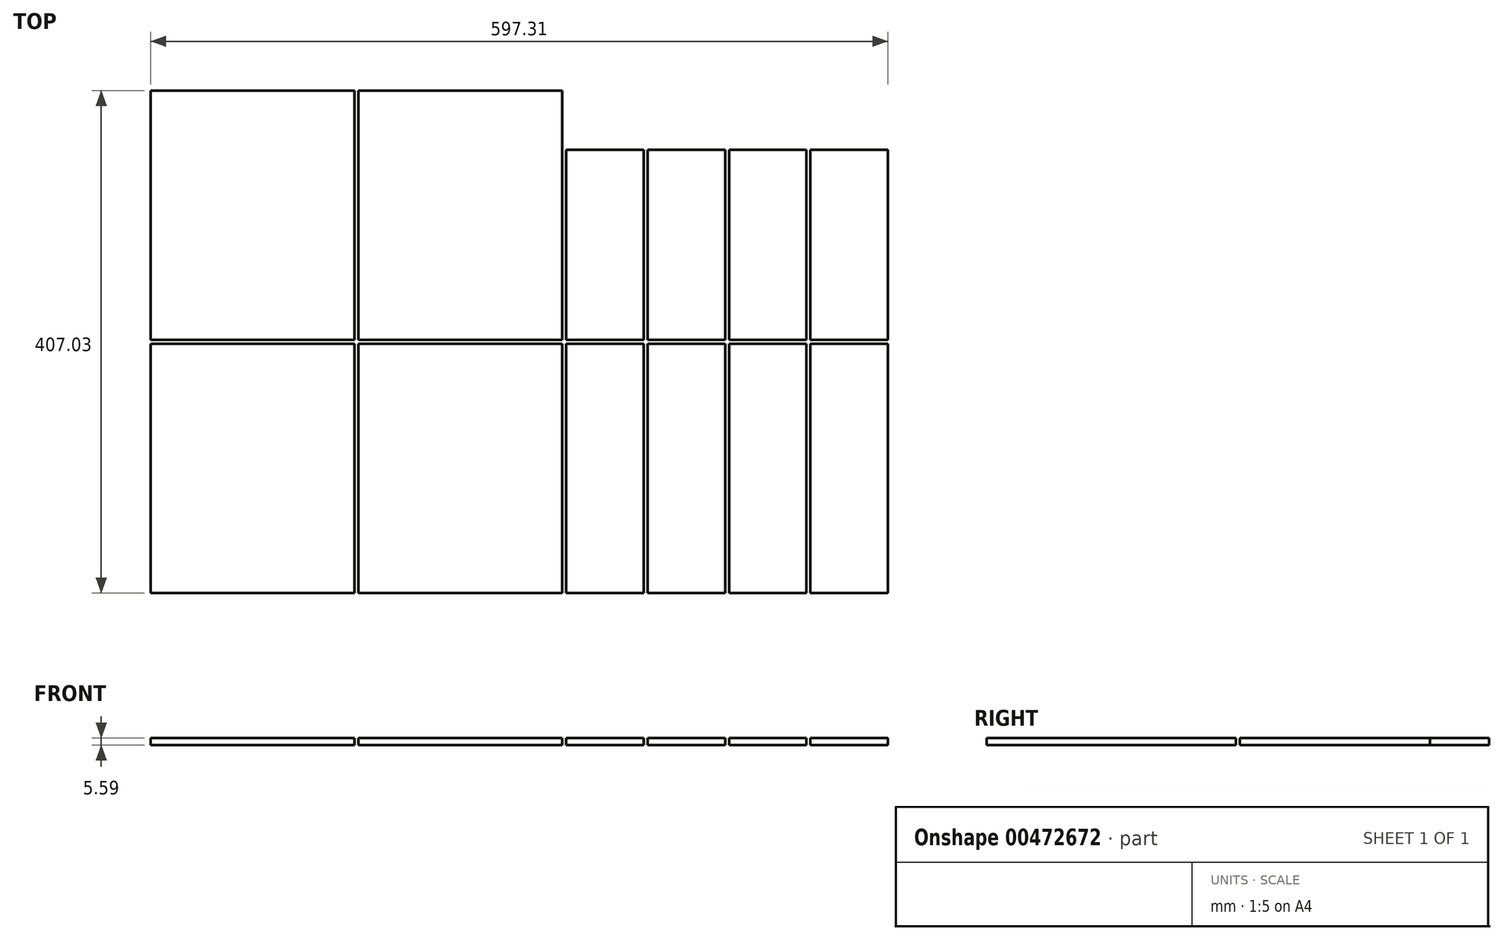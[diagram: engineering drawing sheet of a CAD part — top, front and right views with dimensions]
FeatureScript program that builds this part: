
annotation { "Feature Type Name" : "Feature", "Feature Type Description" : "" }
export const myFeature = defineFeature(function(context is Context, id is Id, definition is map)
    precondition{}
    {
        {
            var Q0;
            Q0=qCreatedBy(makeId("Top.planeOp"),FACE);
            var sketch = newSketch(context, id + "F0", { "sketchPlane" : qUnion([Q0])});
            skLineSegment(sketch, "E0.bottom", {"start": v(0, 0) * mm, "end": v(165.1, 0) * mm});
            skLineSegment(sketch, "E0.top", {"start": v(0, 201.93) * mm, "end": v(165.1, 201.93) * mm});
            skLineSegment(sketch, "E0.left", {"start": v(0, 0) * mm, "end": v(0, 201.93) * mm});
            skLineSegment(sketch, "E0.right", {"start": v(165.1, 0) * mm, "end": v(165.1, 201.93) * mm});
            skLineSegment(sketch, "E1.bottom", {"start": v(168.27, 0) * mm, "end": v(333.38, 0) * mm});
            skLineSegment(sketch, "E1.top", {"start": v(168.27, 201.93) * mm, "end": v(333.38, 201.93) * mm});
            skLineSegment(sketch, "E1.left", {"start": v(168.27, 0) * mm, "end": v(168.27, 201.93) * mm});
            skLineSegment(sketch, "E1.right", {"start": v(333.38, 0) * mm, "end": v(333.37, 201.93) * mm});
            skLineSegment(sketch, "E2.bottom", {"start": v(0, 205.1) * mm, "end": v(165.1, 205.1) * mm});
            skLineSegment(sketch, "E2.top", {"start": v(0, 407.04) * mm, "end": v(165.1, 407.04) * mm});
            skLineSegment(sketch, "E2.left", {"start": v(0, 205.1) * mm, "end": v(0, 407.04) * mm});
            skLineSegment(sketch, "E2.right", {"start": v(165.1, 205.1) * mm, "end": v(165.1, 407.04) * mm});
            skLineSegment(sketch, "E3.bottom", {"start": v(168.27, 205.1) * mm, "end": v(333.37, 205.1) * mm});
            skLineSegment(sketch, "E3.top", {"start": v(168.27, 407.04) * mm, "end": v(333.37, 407.04) * mm});
            skLineSegment(sketch, "E3.left", {"start": v(168.28, 205.1) * mm, "end": v(168.27, 407.04) * mm});
            skLineSegment(sketch, "E3.right", {"start": v(333.37, 205.1) * mm, "end": v(333.37, 407.04) * mm});
            skLineSegment(sketch, "E4", {"start": v(168.27, 205.1) * mm, "end": v(165.1, 205.1) * mm, "construction": true});
            skLineSegment(sketch, "E5", {"start": v(168.27, 205.1) * mm, "end": v(168.27, 201.93) * mm, "construction": true});
            skLineSegment(sketch, "E6.bottom", {"start": v(336.55, 0) * mm, "end": v(399.36, 0) * mm});
            skLineSegment(sketch, "E6.top", {"start": v(336.55, 201.93) * mm, "end": v(399.36, 201.93) * mm});
            skLineSegment(sketch, "E6.left", {"start": v(336.55, 0) * mm, "end": v(336.55, 201.93) * mm});
            skLineSegment(sketch, "E6.right", {"start": v(399.36, 0) * mm, "end": v(399.36, 201.93) * mm});
            skLineSegment(sketch, "E7.bottom", {"start": v(336.55, 205.1) * mm, "end": v(399.36, 205.1) * mm});
            skLineSegment(sketch, "E7.top", {"start": v(336.55, 359.03) * mm, "end": v(399.36, 359.03) * mm});
            skLineSegment(sketch, "E7.left", {"start": v(336.55, 205.1) * mm, "end": v(336.55, 359.03) * mm});
            skLineSegment(sketch, "E7.right", {"start": v(399.36, 205.1) * mm, "end": v(399.36, 359.03) * mm});
            skLineSegment(sketch, "E8.1.0.0", {"start": v(402.53, 359.03) * mm, "end": v(465.34, 359.03) * mm});
            skLineSegment(sketch, "E8.1.0.1", {"start": v(465.34, 205.1) * mm, "end": v(465.34, 359.03) * mm});
            skLineSegment(sketch, "E8.1.0.2", {"start": v(402.53, 205.1) * mm, "end": v(402.53, 359.03) * mm});
            skLineSegment(sketch, "E8.1.0.3", {"start": v(402.53, 205.1) * mm, "end": v(465.34, 205.1) * mm});
            skLineSegment(sketch, "E8.1.0.4", {"start": v(402.53, 201.93) * mm, "end": v(465.34, 201.93) * mm});
            skLineSegment(sketch, "E8.1.0.5", {"start": v(402.53, 0) * mm, "end": v(402.53, 201.93) * mm});
            skLineSegment(sketch, "E8.1.0.6", {"start": v(465.34, 0) * mm, "end": v(465.34, 201.93) * mm});
            skLineSegment(sketch, "E8.1.0.7", {"start": v(402.53, 0) * mm, "end": v(465.34, 0) * mm});
            skLineSegment(sketch, "E8.2.0.0", {"start": v(468.52, 359.03) * mm, "end": v(531.33, 359.03) * mm});
            skLineSegment(sketch, "E8.2.0.1", {"start": v(531.33, 205.1) * mm, "end": v(531.33, 359.03) * mm});
            skLineSegment(sketch, "E8.2.0.2", {"start": v(468.52, 205.1) * mm, "end": v(468.52, 359.03) * mm});
            skLineSegment(sketch, "E8.2.0.3", {"start": v(468.52, 205.1) * mm, "end": v(531.33, 205.1) * mm});
            skLineSegment(sketch, "E8.2.0.4", {"start": v(468.52, 201.93) * mm, "end": v(531.33, 201.93) * mm});
            skLineSegment(sketch, "E8.2.0.5", {"start": v(468.52, 0) * mm, "end": v(468.52, 201.93) * mm});
            skLineSegment(sketch, "E8.2.0.6", {"start": v(531.33, 0) * mm, "end": v(531.33, 201.93) * mm});
            skLineSegment(sketch, "E8.2.0.7", {"start": v(468.52, 0) * mm, "end": v(531.33, 0) * mm});
            skLineSegment(sketch, "E8.3.0.0", {"start": v(534.5, 359.03) * mm, "end": v(597.31, 359.03) * mm});
            skLineSegment(sketch, "E8.3.0.1", {"start": v(597.31, 205.1) * mm, "end": v(597.31, 359.03) * mm});
            skLineSegment(sketch, "E8.3.0.2", {"start": v(534.5, 205.1) * mm, "end": v(534.5, 359.03) * mm});
            skLineSegment(sketch, "E8.3.0.3", {"start": v(534.5, 205.1) * mm, "end": v(597.31, 205.1) * mm});
            skLineSegment(sketch, "E8.3.0.4", {"start": v(534.5, 201.93) * mm, "end": v(597.31, 201.93) * mm});
            skLineSegment(sketch, "E8.3.0.5", {"start": v(534.5, 0) * mm, "end": v(534.5, 201.93) * mm});
            skLineSegment(sketch, "E8.3.0.6", {"start": v(597.31, 0) * mm, "end": v(597.31, 201.93) * mm});
            skLineSegment(sketch, "E8.3.0.7", {"start": v(534.5, 0) * mm, "end": v(597.31, 0) * mm});
            skLineSegment(sketch, "E8.direction1", {"start": v(336.55, 0) * mm, "end": v(402.53, 0) * mm, "construction": true});
            skSolve(sketch);
        }
        {
            var Q0;
            Q0=makeQuery(id+"F0.imprint","IMPRINT",FACE,{"disambiguationData":[TD([[makeQuery(id+"F0.imprint","IMPRINT",EDGE,{"derivedFrom":sQuery(id+"F0.wireOp",EDGE,"E1.bottom")}),1.0]])]});
            var Q1;
            Q1=makeQuery(id+"F0.imprint","IMPRINT",FACE,{"disambiguationData":[TD([[makeQuery(id+"F0.imprint","IMPRINT",EDGE,{"derivedFrom":sQuery(id+"F0.wireOp",EDGE,"E8.3.0.4")}),-1.0]])]});
            var Q2;
            Q2=makeQuery(id+"F0.imprint","IMPRINT",FACE,{"disambiguationData":[TD([[makeQuery(id+"F0.imprint","IMPRINT",EDGE,{"derivedFrom":sQuery(id+"F0.wireOp",EDGE,"E8.1.0.0")}),-1.0]])]});
            var Q3;
            Q3=makeQuery(id+"F0.imprint","IMPRINT",FACE,{"disambiguationData":[TD([[makeQuery(id+"F0.imprint","IMPRINT",EDGE,{"derivedFrom":sQuery(id+"F0.wireOp",EDGE,"E8.1.0.4")}),-1.0]])]});
            var Q4;
            Q4=makeQuery(id+"F0.imprint","IMPRINT",FACE,{"disambiguationData":[TD([[makeQuery(id+"F0.imprint","IMPRINT",EDGE,{"derivedFrom":sQuery(id+"F0.wireOp",EDGE,"E2.bottom")}),1.0]])]});
            var Q5;
            Q5=makeQuery(id+"F0.imprint","IMPRINT",FACE,{"disambiguationData":[TD([[makeQuery(id+"F0.imprint","IMPRINT",EDGE,{"derivedFrom":sQuery(id+"F0.wireOp",EDGE,"E6.bottom")}),1.0]])]});
            var Q6;
            Q6=makeQuery(id+"F0.imprint","IMPRINT",FACE,{"disambiguationData":[TD([[makeQuery(id+"F0.imprint","IMPRINT",EDGE,{"derivedFrom":sQuery(id+"F0.wireOp",EDGE,"E3.bottom")}),1.0]])]});
            var Q7;
            Q7=makeQuery(id+"F0.imprint","IMPRINT",FACE,{"disambiguationData":[TD([[makeQuery(id+"F0.imprint","IMPRINT",EDGE,{"derivedFrom":sQuery(id+"F0.wireOp",EDGE,"E0.bottom")}),1.0]])]});
            var Q8;
            Q8=makeQuery(id+"F0.imprint","IMPRINT",FACE,{"disambiguationData":[TD([[makeQuery(id+"F0.imprint","IMPRINT",EDGE,{"derivedFrom":sQuery(id+"F0.wireOp",EDGE,"E8.2.0.0")}),-1.0]])]});
            var Q9;
            Q9=makeQuery(id+"F0.imprint","IMPRINT",FACE,{"disambiguationData":[TD([[makeQuery(id+"F0.imprint","IMPRINT",EDGE,{"derivedFrom":sQuery(id+"F0.wireOp",EDGE,"E7.bottom")}),1.0]])]});
            var Q10;
            Q10=makeQuery(id+"F0.imprint","IMPRINT",FACE,{"disambiguationData":[TD([[makeQuery(id+"F0.imprint","IMPRINT",EDGE,{"derivedFrom":sQuery(id+"F0.wireOp",EDGE,"E8.2.0.4")}),-1.0]])]});
            var Q11;
            Q11=makeQuery(id+"F0.imprint","IMPRINT",FACE,{"disambiguationData":[TD([[makeQuery(id+"F0.imprint","IMPRINT",EDGE,{"derivedFrom":sQuery(id+"F0.wireOp",EDGE,"E8.3.0.0")}),-1.0]])]});
            extrude(context, id + "F1", {"entities" : qUnion([Q0, Q1, Q2, Q3, Q4, Q5, Q6, Q7, Q8, Q9, Q10, Q11]), "depth" : 5.6 * mm});
        }
    });
